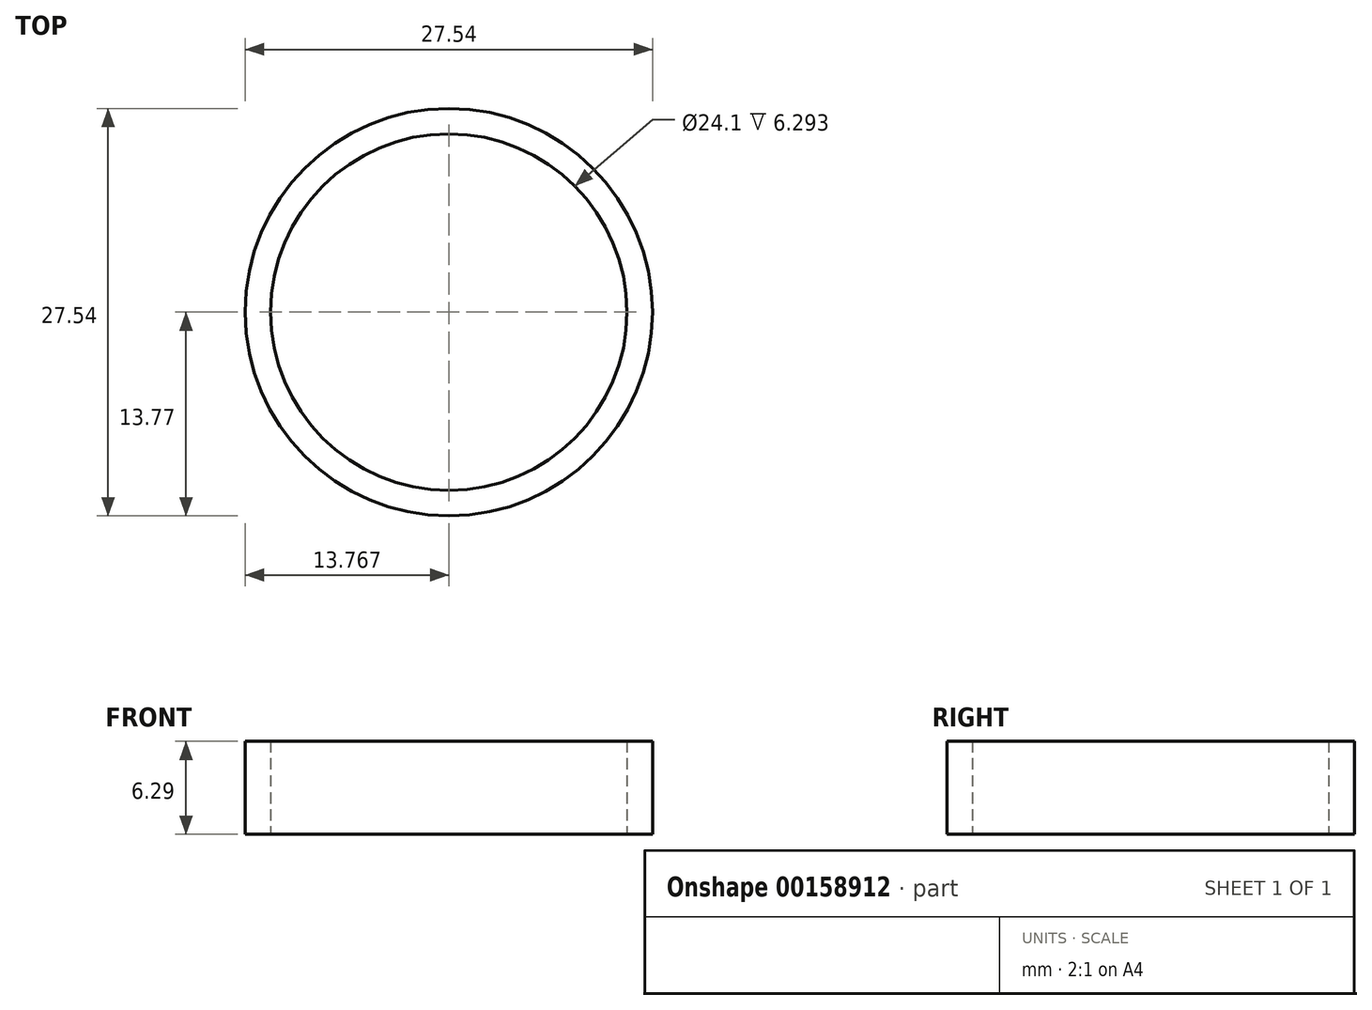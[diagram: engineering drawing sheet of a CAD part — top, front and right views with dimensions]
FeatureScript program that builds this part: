
annotation { "Feature Type Name" : "Feature", "Feature Type Description" : "" }
export const myFeature = defineFeature(function(context is Context, id is Id, definition is map)
    precondition{}
    {
        {
            var Q0;
            Q0=qCreatedBy(makeId("Top.planeOp"),FACE);
            var sketch = newSketch(context, id + "F0", { "sketchPlane" : qUnion([Q0])});
            skCircle(sketch, "E0", {"center": v(-15.02, 0) * mm, "radius": 13.77 * mm});
            skCircle(sketch, "E1", {"center": v(-15.02, 0) * mm, "radius": 12.05 * mm});
            skSolve(sketch);
        }
        {
            var Q0;
            Q0 = qSketchRegion(id + "F0", true);
            extrude(context, id + "F1", {"entities" : qUnion([Q0]), "depth" : 6.3 * mm});
        }
    });
